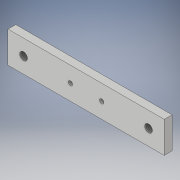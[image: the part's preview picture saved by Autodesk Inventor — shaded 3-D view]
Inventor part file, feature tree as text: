
AUTODESK INVENTOR PART (.ipt)
format: ipt  version: 2019 (Build 230136000, 136)  size: 120,832 bytes
history: native  units: in
note: dims shown in document units (in); Inventor stores cm internally (conversion verified against a paired STEP export)
features: sketch x3, extrude x2, thread x2, hole x1, plane x1, mirror x1
ambient origin geometry x8: Origin, YZ Plane, XZ Plane, XY Plane, X Axis, Y Axis, Z Axis, Center Point
bodies: Solid1 (feature_tree)
feature tree (10):
  extrude  "Extrusion1"  Depth=1.0in
  hole  "Hole1"  [1 undecoded]
  thread  "Thread1"  [1 undecoded]
  plane  "Work Plane1"
  mirror  "Mirror1"
  thread  "Thread2"  [1 undecoded]
  extrude  "Extrusion3"  Depth=0.25in
  sketch  "Sketch1"  dims[d0=5.0in d1=1.0in]
  sketch  "Sketch2"  dims[d2=0.25in d3=0.0in d4=0.5in]
  sketch  "Sketch4"  dims[d5=0.25in d6=0.75in d7=0.375in d8=0.25in d9=0.5635in d10=1.0in d11=0.8108in d12=1.0in d13=0.0in d14=1.0in d15=0.0in d28=0.5in d29=0.5in d30=2.0in d31=2.0in d32=0.14in d33=0.25in d34=0.0in d16=0.375in]
note: 3 required parameter values undecoded (feature->parameter linkage not recoverable at this tier; creation-order binding heuristic only, values carry confidence <= 0.55)
